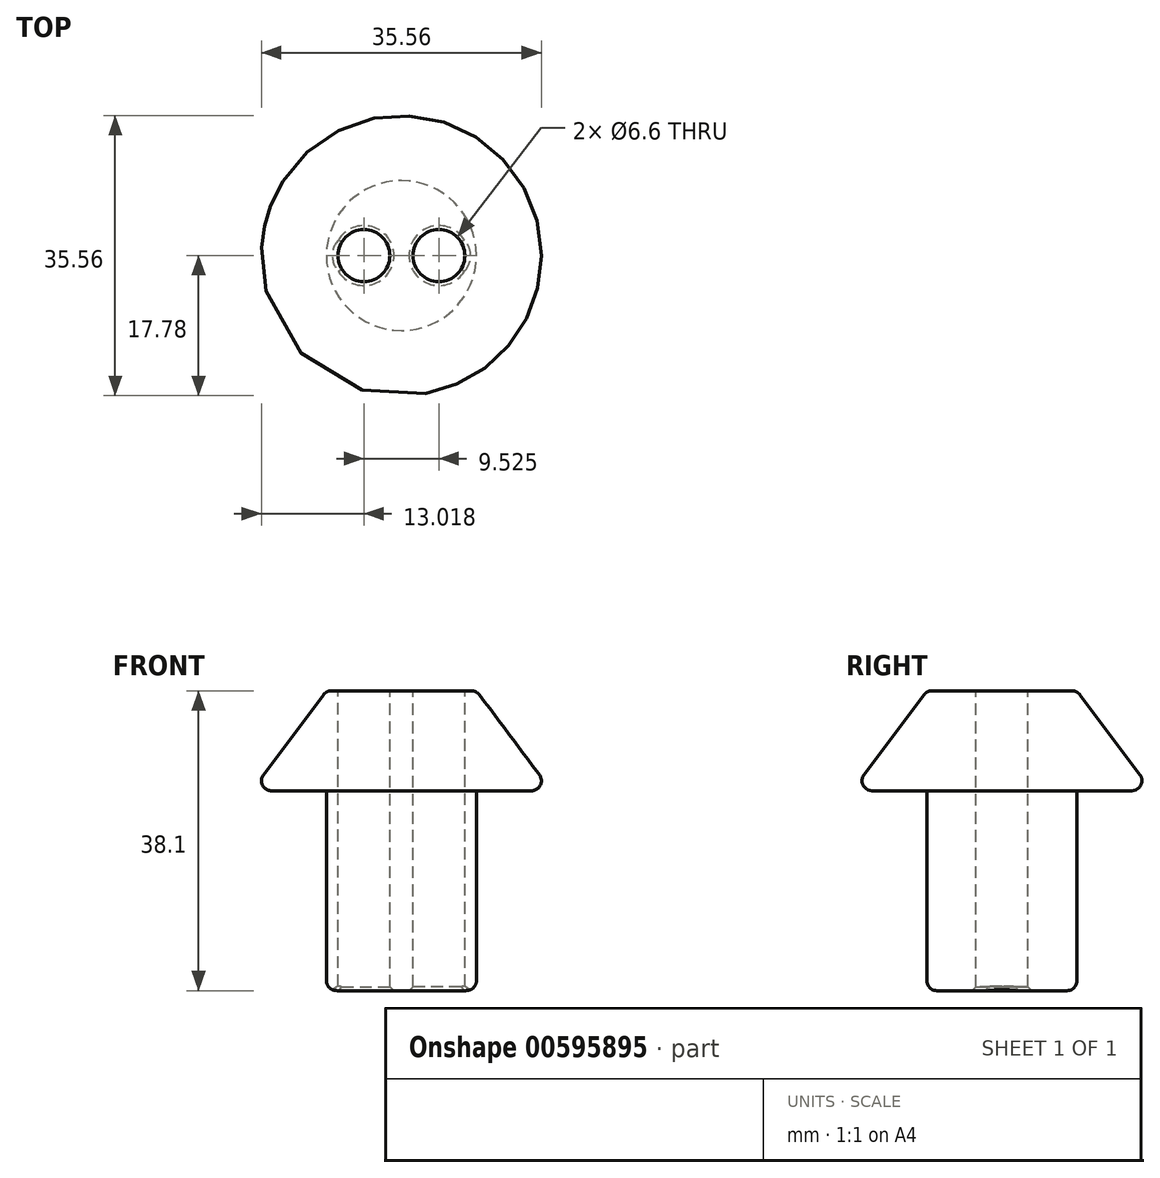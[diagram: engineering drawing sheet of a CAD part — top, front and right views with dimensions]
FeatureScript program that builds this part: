
annotation { "Feature Type Name" : "Feature", "Feature Type Description" : "" }
export const myFeature = defineFeature(function(context is Context, id is Id, definition is map)
    precondition{}
    {
        {
            var Q0;
            Q0=qCreatedBy(makeId("Top.planeOp"),FACE);
            var sketch = newSketch(context, id + "F0", { "sketchPlane" : qUnion([Q0])});
            skCircle(sketch, "E0", {"center": v(0, 0) * mm, "radius": 9.53 * mm});
            skSolve(sketch);
        }
        {
            var Q0;
            Q0=makeQuery(id+"F0.imprint","IMPRINT",FACE,{"disambiguationData":[TD([[makeQuery(id+"F0.imprint","IMPRINT",EDGE,{"derivedFrom":sQuery(id+"F0.wireOp",EDGE,"E0")}),1.0]])]});
            extrude(context, id + "F1", {"entities" : qUnion([Q0]), "depth" : 25.4 * mm, "offsetDistance" : 25.4 * mm});
        }
        {
            var Q0;
            Q0=qCreatedBy(makeId("Front.planeOp"),FACE);
            var sketch = newSketch(context, id + "F2", { "sketchPlane" : qUnion([Q0])});
            skLineSegment(sketch, "E1", {"start": v(0, 25.4) * mm, "end": v(-19.05, 25.4) * mm});
            skLineSegment(sketch, "E2", {"start": v(-19.05, 25.4) * mm, "end": v(-9.52, 38.1) * mm});
            skLineSegment(sketch, "E3", {"start": v(-9.53, 38.1) * mm, "end": v(0, 38.1) * mm});
            skLineSegment(sketch, "E4", {"start": v(0, 38.1) * mm, "end": v(0, 25.4) * mm});
            skLineSegment(sketch, "E5", {"start": v(0, 76.2) * mm, "end": v(0, 0) * mm, "construction": true});
            skSolve(sketch);
        }
        {
            var Q0;
            Q0=makeQuery(id+"F2.imprint","IMPRINT",FACE,{"disambiguationData":[TD([[makeQuery(id+"F2.imprint","IMPRINT",EDGE,{"derivedFrom":sQuery(id+"F2.wireOp",EDGE,"E1")}),-1.0]])]});
            var Q1;
            Q1=sQuery(id+"F2.wireOp",EDGE,"E5");
            revolve(context, id + "F3", {"operationType" : NewBodyOperationType.ADD, "entities" : qUnion([Q0]), "axis" : qUnion([Q1]), "revolveType" : RevolveType.FULL});
        }
        {
            var Q0;
            Q0=makeQuery(id+"F3.opRevolve","SWEPT_FACE",FACE,{"disambiguationData":[OSD([sQuery(id+"F2.wireOp",EDGE,"E3")])]});
            var sketch = newSketch(context, id + "F4", { "sketchPlane" : qUnion([Q0])});
            skCircle(sketch, "E6", {"center": v(-4.76, 0) * mm, "radius": 3.3 * mm});
            skCircle(sketch, "E7", {"center": v(4.76, 0) * mm, "radius": 3.3 * mm});
            skSolve(sketch);
        }
        {
            var Q0;
            Q0 = qSketchRegion(id + "F4", true);
            extrude(context, id + "F5", {"entities" : qUnion([Q0]), "operationType" : NewBodyOperationType.REMOVE, "oppositeDirection" : true, "depth" : 55.55 * mm, "offsetDistance" : 25.4 * mm});
        }
        {
            var Q0;
            Q0=makeQuery(id+"F3.opRevolve","SWEPT_EDGE",EDGE,{"disambiguationData":[OSD([sQuery(id+"F2.wireOp",EDGE,"E1"),sQuery(id+"F2.wireOp",EDGE,"E2")])]});
            var Q1;
            Q1=makeQuery(id+"F3.opRevolve","SWEPT_EDGE",EDGE,{"disambiguationData":[OSD([sQuery(id+"F2.wireOp",EDGE,"E2"),sQuery(id+"F2.wireOp",EDGE,"E3")])]});
            var Q2;
            Q2=makeQuery(id+"F1.opExtrude","CAP_EDGE",EDGE,{"disambiguationData":[OSD([sQuery(id+"F0.wireOp",EDGE,"E0")])],"isStart":true});
            fillet(context, id + "F6", {"entities" : qUnion([Q0, Q1, Q2]), "radius" : 1.27 * mm, "tangentPropagation" : true, "allowEdgeOverflow" : false});
        }
        {
            var Q0;
            Q0=makeQuery(id+"F5.boolean.opBoolean","COPY",EDGE,{"derivedFrom":makeQuery(id+"F5.opExtrude","CAP_EDGE",EDGE,{"disambiguationData":[OSD([sQuery(id+"F4.wireOp",EDGE,"E6")])],"isStart":true})});
            var Q1;
            Q1=makeQuery(id+"F5.boolean.opBoolean","COPY",EDGE,{"derivedFrom":makeQuery(id+"F5.opExtrude","CAP_EDGE",EDGE,{"disambiguationData":[OSD([sQuery(id+"F4.wireOp",EDGE,"E7")])],"isStart":true})});
            var Q2;
            Q2=makeQuery(id+"F5.boolean.opBoolean","INTERSECT",EDGE,{"derivedFrom":[makeQuery(id+"F1.opExtrude","CAP_FACE",FACE,{"disambiguationData":[OSD([sQuery(id+"F0.wireOp",EDGE,"E0")])],"isStart":true}),makeQuery(id+"F5.opExtrude","SWEPT_FACE",FACE,{"disambiguationData":[OSD([sQuery(id+"F4.wireOp",EDGE,"E6")])]})]});
            var Q3;
            Q3=makeQuery(id+"F5.boolean.opBoolean","INTERSECT",EDGE,{"derivedFrom":[makeQuery(id+"F1.opExtrude","CAP_FACE",FACE,{"disambiguationData":[OSD([sQuery(id+"F0.wireOp",EDGE,"E0")])],"isStart":true}),makeQuery(id+"F5.opExtrude","SWEPT_FACE",FACE,{"disambiguationData":[OSD([sQuery(id+"F4.wireOp",EDGE,"E7")])]})]});
            chamfer(context, id + "F7", {"entities" : qUnion([Q0, Q1, Q2, Q3]), "width" : 0.5 * mm, "tangentPropagation" : true});
        }
    });
